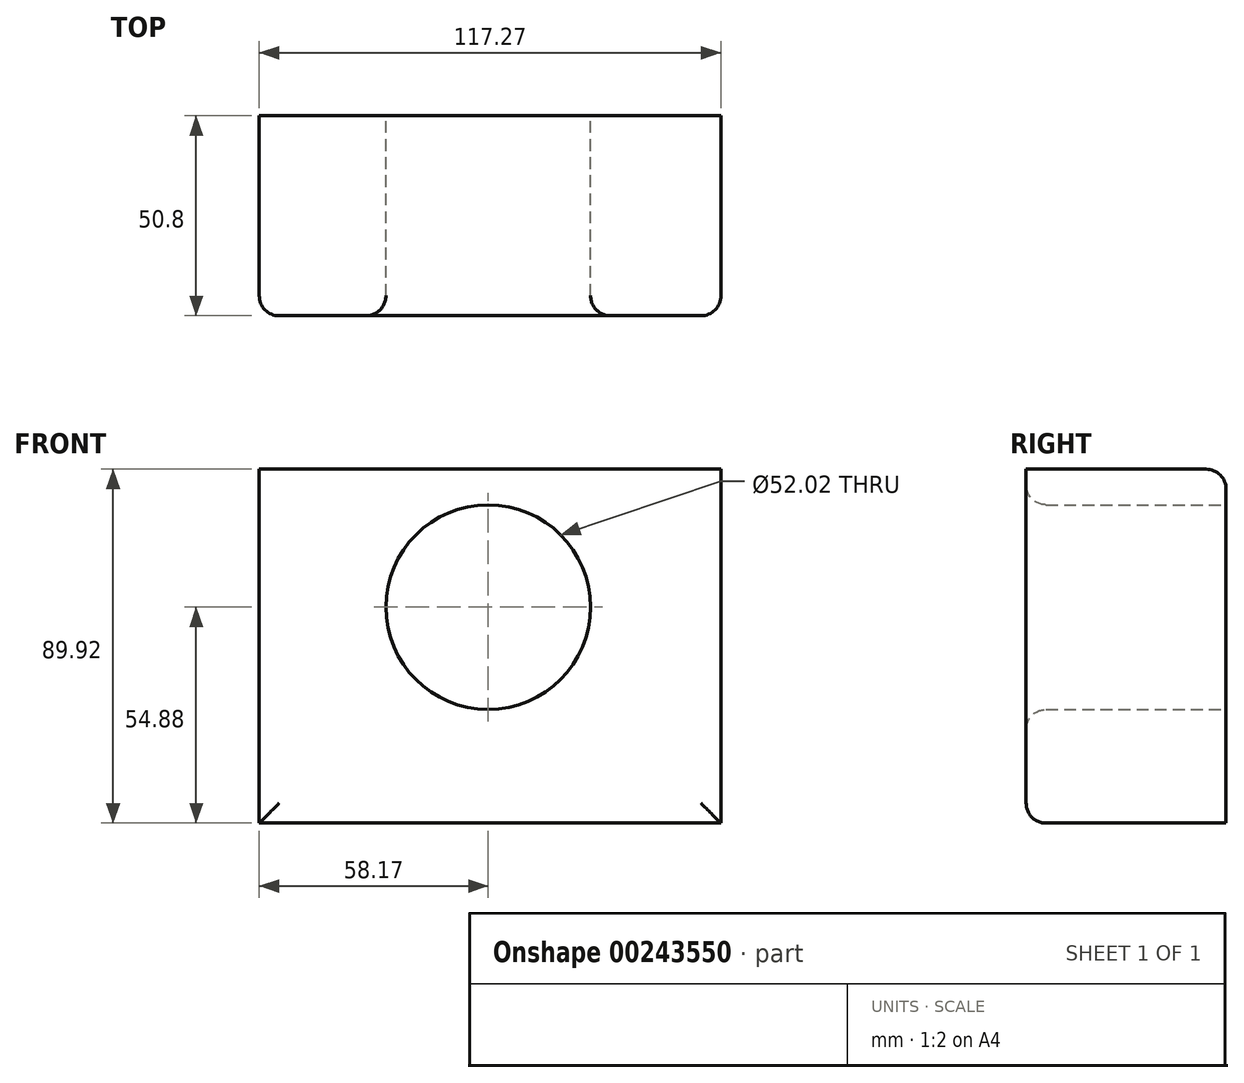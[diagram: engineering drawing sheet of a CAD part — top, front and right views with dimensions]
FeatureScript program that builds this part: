
annotation { "Feature Type Name" : "Feature", "Feature Type Description" : "" }
export const myFeature = defineFeature(function(context is Context, id is Id, definition is map)
    precondition{}
    {
        {
            var Q0;
            Q0=qCreatedBy(makeId("Front.planeOp"),FACE);
            var sketch = newSketch(context, id + "F0", { "sketchPlane" : qUnion([Q0])});
            skLineSegment(sketch, "E0.bottom", {"start": v(-58.17, 35.04) * mm, "end": v(59.1, 35.04) * mm});
            skLineSegment(sketch, "E0.top", {"start": v(-58.17, -54.88) * mm, "end": v(59.1, -54.88) * mm});
            skLineSegment(sketch, "E0.left", {"start": v(-58.17, 35.04) * mm, "end": v(-58.17, -54.88) * mm});
            skLineSegment(sketch, "E0.right", {"start": v(59.1, 35.04) * mm, "end": v(59.1, -54.88) * mm});
            skCircle(sketch, "E1", {"center": v(0, 0) * mm, "radius": 26 * mm});
            skSolve(sketch);
        }
        {
            var Q0;
            Q0 = qSketchRegion(id + "F0", true);
            extrude(context, id + "F1", {"entities" : qUnion([Q0]), "depth" : 50.8 * mm});
        }
        {
            var Q0;
            Q0=makeQuery(id+"F1.opExtrude","CAP_EDGE",EDGE,{"disambiguationData":[OSD([sQuery(id+"F0.wireOp",EDGE,"E0.bottom")])],"isStart":true});
            fillet(context, id + "F2", {"entities" : qUnion([Q0]), "radius" : 5.08 * mm, "tangentPropagation" : true, "allowEdgeOverflow" : false});
        }
        {
            var Q0;
            Q0=makeQuery(id+"F1.opExtrude","CAP_EDGE",EDGE,{"disambiguationData":[OSD([sQuery(id+"F0.wireOp",EDGE,"E0.top")])],"isStart":false});
            var Q1;
            Q1=makeQuery(id+"F1.opExtrude","CAP_EDGE",EDGE,{"disambiguationData":[OSD([sQuery(id+"F0.wireOp",EDGE,"E0.left")])],"isStart":false});
            var Q2;
            Q2=makeQuery(id+"F1.opExtrude","CAP_EDGE",EDGE,{"disambiguationData":[OSD([sQuery(id+"F0.wireOp",EDGE,"E0.right")])],"isStart":false});
            fillet(context, id + "F3", {"entities" : qUnion([Q0, Q1, Q2]), "radius" : 5.08 * mm, "tangentPropagation" : true, "allowEdgeOverflow" : false});
        }
        {
            var Q0;
            Q0=makeQuery(id+"F1.opExtrude","CAP_EDGE",EDGE,{"disambiguationData":[OSD([sQuery(id+"F0.wireOp",EDGE,"E1")])],"isStart":false});
            fillet(context, id + "F4", {"entities" : qUnion([Q0]), "radius" : 5.08 * mm, "tangentPropagation" : true, "allowEdgeOverflow" : false});
        }
    });
